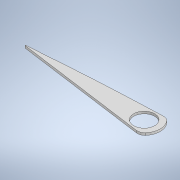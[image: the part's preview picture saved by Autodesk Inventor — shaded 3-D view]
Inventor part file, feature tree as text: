
AUTODESK INVENTOR PART (.ipt)
format: ipt  version: 2022 (Build 260153000, 153)  size: 150,016 bytes
history: native  units: mm
features: extrude x1, sketch x1
ambient origin geometry x8: Origin, YZ Plane, XZ Plane, XY Plane, X Axis, Y Axis, Z Axis, Center Point
bodies: Body1 (feature_tree)
feature tree (2):
  extrude  "Extrusion4"  Depth=8.0mm
  sketch  "Sketch1"  dims[d5=160.0mm d25=6.0mm d26=5.0mm d27=5.0mm d31=34.456mm d41=23.0mm d60=8.0mm d63=2.5mm d64=0.0mm d65=8.0mm]
